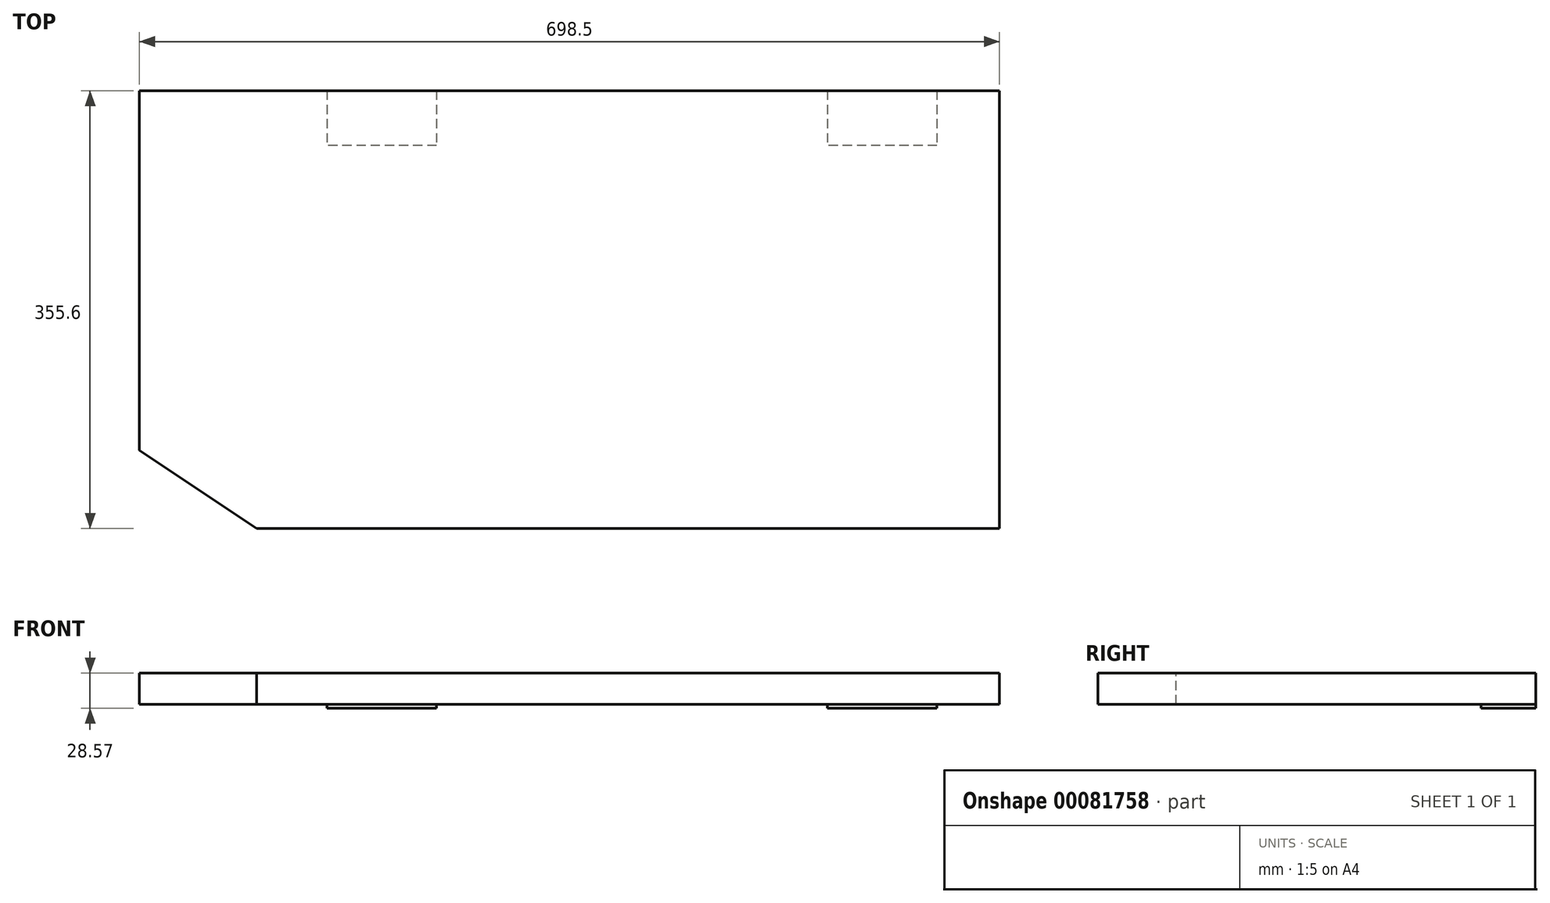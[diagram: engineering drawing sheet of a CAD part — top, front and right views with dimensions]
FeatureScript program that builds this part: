
annotation { "Feature Type Name" : "Feature", "Feature Type Description" : "" }
export const myFeature = defineFeature(function(context is Context, id is Id, definition is map)
    precondition{}
    {
        {
            var Q0;
            Q0=qCreatedBy(makeId("Top.planeOp"),FACE);
            var sketch = newSketch(context, id + "F0", { "sketchPlane" : qUnion([Q0])});
            skLineSegment(sketch, "E0.bottom", {"start": v(349.25, -177.8) * mm, "end": v(-349.25, -177.8) * mm});
            skLineSegment(sketch, "E0.top", {"start": v(349.25, 177.8) * mm, "end": v(-349.25, 177.8) * mm});
            skLineSegment(sketch, "E0.left", {"start": v(349.25, -177.8) * mm, "end": v(349.25, 177.8) * mm});
            skLineSegment(sketch, "E0.right", {"start": v(-349.25, -177.8) * mm, "end": v(-349.25, 177.8) * mm});
            skPoint(sketch, "E0.middle", {"position": v(0, 0) * mm});
            skSolve(sketch);
        }
        {
            var Q0;
            Q0 = qSketchRegion(id + "F0", true);
            extrude(context, id + "F1", {"entities" : qUnion([Q0]), "depth" : 25.4 * mm});
        }
        {
            var Q0;
            Q0=makeQuery(id+"F1.opExtrude","CAP_FACE",FACE,{"disambiguationData":[OSD([sQuery(id+"F0.wireOp",EDGE,"E0.bottom"),sQuery(id+"F0.wireOp",EDGE,"E0.top"),sQuery(id+"F0.wireOp",EDGE,"E0.left"),sQuery(id+"F0.wireOp",EDGE,"E0.right")])],"isStart":false});
            var sketch = newSketch(context, id + "F2", { "sketchPlane" : qUnion([Q0])});
            skLineSegment(sketch, "E1", {"start": v(-349.25, -114.3) * mm, "end": v(-254, -177.8) * mm});
            skLineSegment(sketch, "E2", {"start": v(-254, -177.8) * mm, "end": v(-349.25, -177.8) * mm});
            skLineSegment(sketch, "E3", {"start": v(-349.25, -177.8) * mm, "end": v(-349.25, -114.3) * mm});
            skSolve(sketch);
        }
        {
            var Q0;
            Q0 = qSketchRegion(id + "F2", true);
            extrude(context, id + "F3", {"entities" : qUnion([Q0]), "operationType" : NewBodyOperationType.REMOVE, "endBound" : BoundingType.THROUGH_ALL, "oppositeDirection" : true, "depth" : 25.4 * mm});
        }
        {
            var Q0;
            Q0=makeQuery(id+"F1.opExtrude","CAP_FACE",FACE,{"disambiguationData":[OSD([sQuery(id+"F0.wireOp",EDGE,"E0.bottom"),sQuery(id+"F0.wireOp",EDGE,"E0.top"),sQuery(id+"F0.wireOp",EDGE,"E0.left"),sQuery(id+"F0.wireOp",EDGE,"E0.right")])],"isStart":true});
            var sketch = newSketch(context, id + "F4", { "sketchPlane" : qUnion([Q0])});
            skLineSegment(sketch, "E4.bottom", {"start": v(298.45, -177.8) * mm, "end": v(209.55, -177.8) * mm});
            skLineSegment(sketch, "E4.top", {"start": v(298.45, -133.35) * mm, "end": v(209.55, -133.35) * mm});
            skLineSegment(sketch, "E4.left", {"start": v(298.45, -177.8) * mm, "end": v(298.45, -133.35) * mm});
            skLineSegment(sketch, "E4.right", {"start": v(209.55, -177.8) * mm, "end": v(209.55, -133.35) * mm});
            skLineSegment(sketch, "E5.bottom", {"start": v(-107.95, -177.8) * mm, "end": v(-196.85, -177.8) * mm});
            skLineSegment(sketch, "E5.top", {"start": v(-107.95, -133.35) * mm, "end": v(-196.85, -133.35) * mm});
            skLineSegment(sketch, "E5.left", {"start": v(-107.95, -177.8) * mm, "end": v(-107.95, -133.35) * mm});
            skLineSegment(sketch, "E5.right", {"start": v(-196.85, -177.8) * mm, "end": v(-196.85, -133.35) * mm});
            skSolve(sketch);
        }
        {
            var Q0;
            Q0 = qSketchRegion(id + "F4", true);
            extrude(context, id + "F5", {"entities" : qUnion([Q0]), "operationType" : NewBodyOperationType.ADD, "depth" : 3.17 * mm});
        }
    });
